# Revit family: Faucet-Lavatory-KOHLER-Willamette-K-R99901
name_source: partatom
category: Plumbing Fixtures
revit_build: Autodesk Revit 2015 (Build: 20140606_1530(x64)
units: mm (PartAtom-declared; Revit-internal decimal feet)

## types (3) — shared parameters
ADA Compliant = Yes
Assembly Code = D2010
CW Connection = Yes
Cold Water Inlet = Cold Water Inlet
Date Modified = 05/04/2018
Default Elevation = 36"
Drain Included = Yes
HW Connection = Yes
Height = 5 1/2"
Hot Water Inlet = Hot Water Inlet
Length = 6"
Manufacturer = KOHLER Co.
MasterFormat 1995 = 15410
MasterFormat 2004 = 22.41.39
Material = Premium Metal
Pressure = 60.00 psi
Product Documentation Link = http://www.us.kohler.com
Product Name = Willamette
Product Page URL = http://www.us.kohler.com
Spout Reach = 6"
URL = https://www.us.kohler.com
Vent Connection = No
Waste Connection = No
Waste Water Outlet = Waste Water Outlet

## per-type parameters (varying)
| type | Description | Finish | Flow Rate | Model | Type |
| 1.2 gpm faucet, CP-Polished Chrome | Widespread bathroom sink faucet, 1.2 gpm | Kohler-Metal-CP-Polished_Chrome | 1 GPM | K-R99901-4D1-CP | 1 |
| 1.2 gpm faucet, BN-Vibrant Brushed Nickel | Widespread bathroom sink faucet, 1.2 gpm | Kohler-Metal-BN-Vibrant_Brushed_Nickel | 1 GPM | K-R99901-4D1-BN | 2 |
| 1.5 gpm faucet, CP-Polished Chrome | widespread bathroom sink faucet, 1.5 gpm | Kohler-Metal-CP-Polished_Chrome | 2 GPM | K-R99901-4D-CP | 3 |

## geometry (parser evidence)
native form markers: Blend x2, Sweep x7
no freeform markers — native parametric forms only
